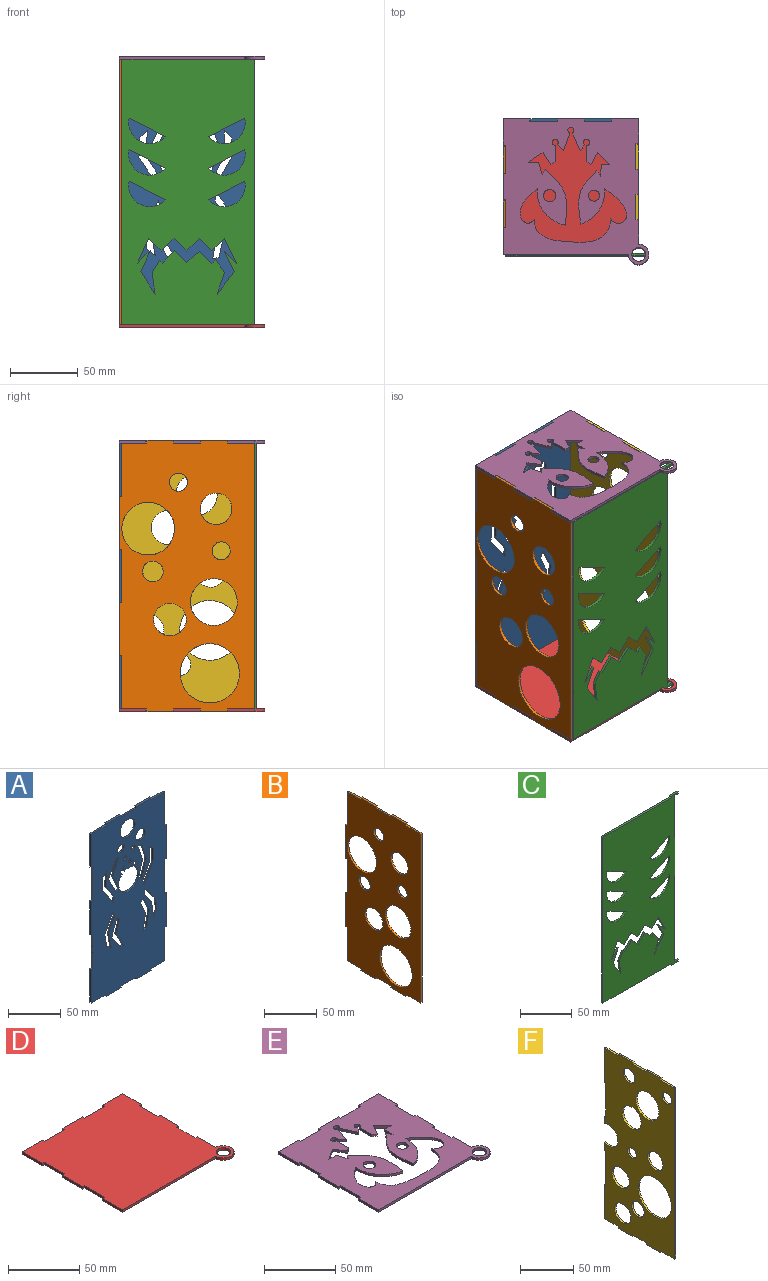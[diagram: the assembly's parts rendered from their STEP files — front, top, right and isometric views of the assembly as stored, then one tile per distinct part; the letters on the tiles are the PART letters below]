
ASSEMBLY  parts=6 mates=5
PART A: 102 faces, bbox 100x2x200 mm
  f0: plane 200x100mm, normal (0,-1,0), area 16666.3mm2, adj f2,f3,f4,f5,f6,f7,f8,f9
  f1: plane 200x100mm, normal (0,1,0), area 16666.3mm2, adj f2,f3,f4,f5,f6,f7,f8,f9
  f2: plane 39.2x2mm, normal (-1,0,0), area 78.4mm2, adj f0,f1,f33,f35
  f3: plane 39.2x2mm, normal (-1,0,0), area 78.4mm2, adj f0,f1,f16,f32
  f4: plane 39.6x2mm, normal (1,0,0), area 79.2mm2, adj f0,f1,f25,f28
  f5: plane 39.6x2mm, normal (1,0,0), area 79.2mm2, adj f0,f1,f26,f30
  f6: plane 17.8x2mm, normal (0,0,-1), area 35.6mm2, adj f0,f1,f15,f31
  f7: plane 39.2x2mm, normal (-1,0,0), area 78.4mm2, adj f0,f1,f24,f36
  f8: plane 20.4x2mm, normal (0,0,1), area 40.8mm2, adj f0,f1,f20,f23
  f9: plane 20.4x2mm, normal (0,0,1), area 40.8mm2, adj f0,f1,f18,f22
  f10: plane 20.4x2mm, normal (0,0,-1), area 40.8mm2, adj f0,f1,f12,f17
  f11: plane 20.4x2mm, normal (0,0,-1), area 40.8mm2, adj f0,f1,f14,f15
  f12: plane 2x2mm, normal (1,0,0), area 4mm2, adj f0,f1,f10,f13
  f13: plane 19.6x2mm, normal (0,0,-1), area 39.2mm2, adj f0,f1,f12,f14
  f14: plane 2x2mm, normal (-1,0,0), area 4mm2, adj f0,f1,f11,f13
  f15: plane 2x2mm, normal (1,0,0), area 4mm2, adj f0,f1,f6,f11
  f16: plane 19.8x2mm, normal (0,0,-1), area 39.6mm2, adj f0,f1,f3,f17
  f17: plane 2x2mm, normal (-1,0,0), area 4mm2, adj f0,f1,f10,f16
  f18: plane 2x2mm, normal (-1,0,0), area 4mm2, adj f0,f1,f9,f19
  f19: plane 19.6x2mm, normal (0,0,1), area 39.2mm2, adj f0,f1,f18,f20
  f20: plane 2x2mm, normal (1,0,0), area 4mm2, adj f0,f1,f8,f19
  f21: plane 17.8x2mm, normal (0,0,1), area 35.6mm2, adj f0,f1,f22,f29
  f22: plane 2x2mm, normal (1,0,0), area 4mm2, adj f0,f1,f9,f21
  f23: plane 2x2mm, normal (-1,0,0), area 4mm2, adj f0,f1,f8,f24
  f24: plane 19.8x2mm, normal (0,0,1), area 39.6mm2, adj f0,f1,f7,f23
  f25: plane 2x2mm, normal (0,0,-1), area 4mm2, adj f0,f1,f4,f27
  f26: plane 2x2mm, normal (0,0,1), area 4mm2, adj f0,f1,f5,f27
  f27: plane 38.8x2mm, normal (1,0,0), area 77.6mm2, adj f0,f1,f25,f26
  f28: plane 2x2mm, normal (0,0,1), area 4mm2, adj f0,f1,f4,f29
  f29: plane 39x2mm, normal (1,0,0), area 78mm2, adj f0,f1,f21,f28
  f30: plane 2x2mm, normal (0,0,-1), area 4mm2, adj f0,f1,f5,f31
  f31: plane 39x2mm, normal (1,0,0), area 78mm2, adj f0,f1,f6,f30
  f32: plane 2x2mm, normal (0,0,1), area 4mm2, adj f0,f1,f3,f34
  f33: plane 2x2mm, normal (0,0,-1), area 4mm2, adj f0,f1,f2,f34
  f34: plane 39.2x2mm, normal (-1,0,0), area 78.4mm2, adj f0,f1,f32,f33
  f35: plane 2x2mm, normal (0,0,1), area 4mm2, adj f0,f1,f2,f37
  f36: plane 2x2mm, normal (0,0,-1), area 4mm2, adj f0,f1,f7,f37
  f37: plane 39.2x2mm, normal (-1,0,0), area 78.4mm2, adj f0,f1,f35,f36
  f38: plane 4.08x3.06mm, normal (-0.8,0,0.6), area 10.2mm2, adj f0,f1,f39,f47
  f39: cylinder r=13.45mm len=26.89mm, axis (0,1,0), area 129.9mm2, adj f0,f1,f38,f40
  f40: plane 4.08x2.66mm, normal (0.84,0,0.55), area 9.7mm2, adj f0,f1,f39,f41
  f41: plane 6.45x5.23mm, normal (0.63,0,-0.78), area 16.6mm2, adj f0,f1,f40,f42
  f42: plane 5.68x2.93mm, normal (-0.89,0,0.46), area 12.8mm2, adj f0,f1,f41,f43
  f43: plane 2.68x2mm, normal (-0.46,0,-0.89), area 6mm2, adj f0,f1,f42,f44
  f44: cylinder r=13.45mm len=10.78mm, axis (0,1,0), area 22.2mm2, adj f0,f1,f43,f45
  f45: plane 2.61x2mm, normal (0.46,0,-0.89), area 5.9mm2, adj f0,f1,f44,f46
  f46: plane 5.68x2.98mm, normal (0.89,0,0.46), area 12.8mm2, adj f0,f1,f45,f47
  f47: plane 6.98x5.23mm, normal (-0.6,0,-0.8), area 17.4mm2, adj f0,f1,f38,f46
  f48: cylinder r=2.47mm len=4.94mm, axis (0,1,0), area 31.1mm2, adj f0,f1
  f49: cylinder r=2.82mm len=5.64mm, axis (0,1,0), area 35.4mm2, adj f0,f1
  f50: cylinder r=4.52mm len=9.03mm, axis (0,1,0), area 56.8mm2, adj f0,f1
  f51: cylinder r=10.15mm len=20.29mm, axis (0,1,0), area 127.5mm2, adj f0,f1
  f52: cylinder r=1.85mm len=3.69mm, axis (0,1,0), area 23.2mm2, adj f0,f1
  f53: cylinder r=6.54mm len=13.08mm, axis (0,1,0), area 82.2mm2, adj f0,f1
  f54: cylinder r=21.63mm len=3.26mm, axis (0,1,0), area 9mm2, adj f0,f1,f55,f59
  f55: plane 20.47x10.75mm, normal (0.89,0,0.46), area 46.2mm2, adj f0,f1,f54,f56
  f56: plane 18.83x9.64mm, normal (0.89,0,-0.46), area 42.3mm2, adj f0,f1,f55,f57
  f57: plane 4.3x2mm, normal (0.15,0,-0.99), area 8.7mm2, adj f0,f1,f56,f58
  f58: plane 18.83x8.03mm, normal (-0.92,0,0.39), area 40.9mm2, adj f0,f1,f57,f59
  f59: plane 18.05x8.1mm, normal (-0.91,0,-0.41), area 39.6mm2, adj f0,f1,f54,f58
  f60: cylinder r=21.63mm len=3.98mm, axis (0,1,0), area 11.3mm2, adj f0,f1,f61,f65
  f61: plane 18.05x5.28mm, normal (0.96,0,-0.28), area 37.6mm2, adj f0,f1,f60,f62
  f62: plane 18.83x6.04mm, normal (0.95,0,0.31), area 39.5mm2, adj f0,f1,f61,f63
  f63: plane 4.89x2mm, normal (-0.13,0,-0.99), area 9.9mm2, adj f0,f1,f62,f64
  f64: plane 18.83x6.47mm, normal (-0.95,0,-0.32), area 39.8mm2, adj f0,f1,f63,f65
  f65: plane 21.36x6.62mm, normal (-0.96,0,0.3), area 44.7mm2, adj f0,f1,f60,f64
  f66: plane 18.12x8.28mm, normal (-0.91,0,-0.42), area 39.8mm2, adj f0,f1,f67,f71
  f67: plane 19.5x4mm, normal (-0.98,0,0.2), area 39.8mm2, adj f0,f1,f66,f68
  f68: plane 4.77x2mm, normal (-0.26,0,0.97), area 9.9mm2, adj f0,f1,f67,f69
  f69: plane 19.45x3.58mm, normal (0.98,0,-0.18), area 39.5mm2, adj f0,f1,f68,f70
  f70: plane 14.53x6.36mm, normal (0.92,0,0.4), area 31.7mm2, adj f0,f1,f69,f71
  f71: cylinder r=21.63mm len=4.92mm, axis (0,1,0), area 11.9mm2, adj f0,f1,f66,f70
  f72: plane 19.04x14.27mm, normal (-0.8,0,-0.6), area 47.6mm2, adj f0,f1,f73,f77
  f73: plane 14.25x2mm, normal (-0.99,0,-0.13), area 28.7mm2, adj f0,f1,f72,f74
  f74: plane 5.85x4.73mm, normal (-0.78,0,0.63), area 15.1mm2, adj f0,f1,f73,f75
  f75: plane 18.75x2.42mm, normal (0.99,0,0.13), area 37.8mm2, adj f0,f1,f74,f76
  f76: plane 14.05x9.72mm, normal (0.82,0,0.57), area 34.2mm2, adj f0,f1,f75,f77
  f77: cylinder r=21.63mm len=6.34mm, axis (0,1,0), area 12.8mm2, adj f0,f1,f72,f76
  f78: cylinder r=21.63mm len=5.19mm, axis (0,1,0), area 11.2mm2, adj f0,f1,f79,f83
  f79: plane 16.73x8.65mm, normal (0.89,0,-0.46), area 37.7mm2, adj f0,f1,f78,f80
  f80: plane 18.91x2mm, normal (1,0,0), area 37.8mm2, adj f0,f1,f79,f81
  f81: plane 5.44x5.2mm, normal (-0.69,0,-0.72), area 15.1mm2, adj f0,f1,f80,f82
  f82: plane 14.37x2mm, normal (-1,0,0), area 28.7mm2, adj f0,f1,f81,f83
  f83: plane 21.27x12.03mm, normal (-0.87,0,0.49), area 48.9mm2, adj f0,f1,f78,f82
  f84: plane 14.38x2.62mm, normal (0.98,0,0.18), area 29.2mm2, adj f0,f1,f85,f89
  f85: plane 21.56x11.05mm, normal (0.89,0,-0.46), area 48.5mm2, adj f0,f1,f84,f86
  f86: cylinder r=21.63mm len=5.63mm, axis (0,1,0), area 12.2mm2, adj f0,f1,f85,f87
  f87: plane 16.15x8.13mm, normal (-0.89,0,0.45), area 36.2mm2, adj f0,f1,f86,f88
  f88: plane 18.63x3.4mm, normal (-0.98,0,-0.18), area 37.9mm2, adj f0,f1,f87,f89
  f89: plane 6.04x4.46mm, normal (0.59,0,0.8), area 15mm2, adj f0,f1,f84,f88
  f90: cylinder r=21.63mm len=5.19mm, axis (0,1,0), area 11.2mm2, adj f0,f1,f91,f95
  f91: plane 21.04x14.45mm, normal (0.82,0,0.57), area 51mm2, adj f0,f1,f90,f92
  f92: plane 14.6x2mm, normal (1,0,-0.05), area 29.2mm2, adj f0,f1,f91,f93
  f93: plane 5.42x5.2mm, normal (0.69,0,-0.72), area 15mm2, adj f0,f1,f92,f94
  f94: plane 18.91x2mm, normal (-1,0,0.05), area 37.9mm2, adj f0,f1,f93,f95
  f95: plane 16.73x11.31mm, normal (-0.83,0,-0.56), area 40.4mm2, adj f0,f1,f90,f94
  f96: plane 17.44x11.97mm, normal (0.82,0,0.57), area 42.3mm2, adj f0,f1,f97,f101
  f97: plane 19.14x7.1mm, normal (0.94,0,-0.35), area 40.8mm2, adj f0,f1,f96,f98
  f98: cylinder r=21.63mm len=3.67mm, axis (0,1,0), area 9.6mm2, adj f0,f1,f97,f99
  f99: plane 15.95x4.82mm, normal (-0.96,0,0.29), area 33.3mm2, adj f0,f1,f98,f100
  f100: plane 17.65x10.38mm, normal (-0.86,0,-0.51), area 40.9mm2, adj f0,f1,f99,f101
  f101: plane 4.35x2mm, normal (0.02,0,1), area 8.7mm2, adj f0,f1,f96,f100
PART B: 38 faces, bbox 2x100x200 mm
  f0: plane 39.6x2mm, normal (0,1,0), area 79.2mm2, adj f3,f4,f23,f29
  f1: plane 39.6x2mm, normal (0,1,0), area 79.2mm2, adj f3,f4,f25,f26
  f2: plane 17.8x2mm, normal (0,0,-1), area 35.6mm2, adj f3,f4,f13,f28
  f3: plane 200x100mm, normal (1,0,0), area 14548.8mm2, adj f0,f1,f2,f5,f6,f7,f8,f9
  f4: plane 200x100mm, normal (-1,0,0), area 14548.8mm2, adj f0,f1,f2,f5,f6,f7,f8,f9
  f5: plane 20.4x2mm, normal (0,0,1), area 40.8mm2, adj f3,f4,f18,f21
  f6: plane 20.4x2mm, normal (0,0,1), area 40.8mm2, adj f3,f4,f16,f20
  f7: plane 196x2mm, normal (0,-1,0), area 392mm2, adj f3,f4,f14,f22
  f8: plane 20.4x2mm, normal (0,0,-1), area 40.8mm2, adj f3,f4,f10,f15
  f9: plane 20.4x2mm, normal (0,0,-1), area 40.8mm2, adj f3,f4,f12,f13
  f10: plane 2x2mm, normal (0,1,0), area 4mm2, adj f3,f4,f8,f11
  f11: plane 19.6x2mm, normal (0,0,-1), area 39.2mm2, adj f3,f4,f10,f12
  f12: plane 2x2mm, normal (0,-1,0), area 4mm2, adj f3,f4,f9,f11
  f13: plane 2x2mm, normal (0,1,0), area 4mm2, adj f2,f3,f4,f9
  f14: plane 19.8x2mm, normal (0,0,-1), area 39.6mm2, adj f3,f4,f7,f15
  f15: plane 2x2mm, normal (0,-1,0), area 4mm2, adj f3,f4,f8,f14
  f16: plane 2x2mm, normal (0,-1,0), area 4mm2, adj f3,f4,f6,f17
  f17: plane 19.6x2mm, normal (0,0,1), area 39.2mm2, adj f3,f4,f16,f18
  f18: plane 2x2mm, normal (0,1,0), area 4mm2, adj f3,f4,f5,f17
  f19: plane 17.8x2mm, normal (0,0,1), area 35.6mm2, adj f3,f4,f20,f27
  f20: plane 2x2mm, normal (0,1,0), area 4mm2, adj f3,f4,f6,f19
  f21: plane 2x2mm, normal (0,-1,0), area 4mm2, adj f3,f4,f5,f22
  f22: plane 19.8x2mm, normal (0,0,1), area 39.6mm2, adj f3,f4,f7,f21
  f23: plane 2x2mm, normal (0,0,1), area 4mm2, adj f0,f3,f4,f24
  f24: plane 38.8x2mm, normal (0,1,0), area 77.6mm2, adj f3,f4,f23,f25
  f25: plane 2x2mm, normal (0,0,-1), area 4mm2, adj f1,f3,f4,f24
  f26: plane 2x2mm, normal (0,0,1), area 4mm2, adj f1,f3,f4,f27
  f27: plane 39x2mm, normal (0,1,0), area 78mm2, adj f3,f4,f19,f26
  f28: plane 39x2mm, normal (0,1,0), area 78mm2, adj f2,f3,f4,f29
  f29: plane 2x2mm, normal (0,0,-1), area 4mm2, adj f0,f3,f4,f28
  f30: cylinder r=11.7mm len=23.4mm, axis (-1,0,0), area 147mm2, adj f3,f4
  f31: cylinder r=7.63mm len=15.27mm, axis (-1,0,0), area 95.9mm2, adj f3,f4
  f32: cylinder r=17.3mm len=34.6mm, axis (-1,0,0), area 217.4mm2, adj f3,f4
  f33: cylinder r=21.87mm len=43.75mm, axis (-1,0,0), area 274.9mm2, adj f3,f4
  f34: cylinder r=19.45mm len=38.89mm, axis (-1,0,0), area 244.4mm2, adj f3,f4
  f35: cylinder r=6.71mm len=13.42mm, axis (-1,0,0), area 84.3mm2, adj f3,f4
  f36: cylinder r=6.6mm len=13.2mm, axis (-1,0,0), area 82.9mm2, adj f3,f4
  f37: cylinder r=12.07mm len=24.15mm, axis (-1,0,0), area 151.7mm2, adj f3,f4
PART C: 50 faces, bbox 103x2x200 mm
  f0: cylinder r=15.53mm len=27.04mm, axis (0,1,0), area 81.3mm2, adj f47,f48,f49
  f1: cylinder r=15.53mm len=27.04mm, axis (0,1,0), area 81.3mm2, adj f40,f48,f49
  f2: plane 16.09x5.46mm, normal (0.95,0,-0.32), area 34mm2, adj f3,f41,f48,f49
  f3: plane 9.4x6.49mm, normal (0.82,0,0.57), area 22.8mm2, adj f2,f4,f48,f49
  f4: plane 2.84x2.79mm, normal (-0.7,0,0.71), area 8mm2, adj f3,f5,f48,f49
  f5: plane 9.17x9.02mm, normal (0.71,0,0.7), area 25.7mm2, adj f4,f6,f48,f49
  f6: plane 9.45x8.73mm, normal (-0.68,0,0.73), area 25.7mm2, adj f5,f7,f48,f49
  f7: plane 8.97x8.82mm, normal (0.71,0,0.7), area 25.2mm2, adj f6,f8,f48,f49
  f8: plane 9.27x9.11mm, normal (-0.7,0,0.71), area 26mm2, adj f7,f9,f48,f49
  f9: plane 2.07x2.04mm, normal (0.71,0,0.7), area 5.8mm2, adj f8,f10,f48,f49
  f10: plane 8.98x5.53mm, normal (-0.85,0,0.52), area 21.1mm2, adj f9,f11,f48,f49
  f11: plane 16.09x2.22mm, normal (-0.99,0,-0.14), area 32.5mm2, adj f10,f12,f48,f49
  f12: plane 16.71x10.37mm, normal (0.85,0,0.53), area 39.3mm2, adj f11,f13,f48,f49
  f13: plane 15.41x6.75mm, normal (0.92,0,-0.4), area 33.6mm2, adj f12,f14,f48,f49
  f14: plane 9.27x9.11mm, normal (-0.7,0,0.71), area 26mm2, adj f13,f15,f48,f49
  f15: plane 18.28x8.1mm, normal (0.91,0,-0.41), area 40mm2, adj f14,f16,f48,f49
  f16: plane 9.42x9.26mm, normal (-0.71,0,-0.7), area 26.4mm2, adj f15,f17,f48,f49
  f17: plane 9.58x9.42mm, normal (0.7,0,-0.71), area 26.9mm2, adj f16,f18,f48,f49
  f18: plane 9.42x9.26mm, normal (-0.71,0,-0.7), area 26.4mm2, adj f17,f19,f48,f49
  f19: plane 9.58x9.42mm, normal (0.7,0,-0.71), area 26.9mm2, adj f18,f20,f48,f49
  f20: plane 9.17x9.02mm, normal (-0.71,0,-0.7), area 25.7mm2, adj f19,f21,f48,f49
  f21: plane 9.33x9.17mm, normal (0.7,0,-0.71), area 26.2mm2, adj f20,f22,f48,f49
  f22: plane 18.59x9.02mm, normal (-0.9,0,-0.44), area 41.3mm2, adj f21,f23,f48,f49
  f23: plane 9.17x9.02mm, normal (0.71,0,0.7), area 25.7mm2, adj f22,f24,f48,f49
  f24: plane 15.16x7.35mm, normal (-0.9,0,-0.44), area 33.7mm2, adj f23,f41,f48,f49
  f25: cylinder r=15.53mm len=27.04mm, axis (0,1,0), area 81.3mm2, adj f42,f48,f49
  f26: cylinder r=15.53mm len=27.04mm, axis (0,1,0), area 81.3mm2, adj f43,f48,f49
  f27: cylinder r=15.53mm len=27.04mm, axis (0,1,0), area 81.3mm2, adj f44,f48,f49
  f28: cylinder r=15.53mm len=27.04mm, axis (0,1,0), area 81.3mm2, adj f45,f48,f49
  f29: plane 2x1.99mm, normal (-1,0,0), area 4mm2, adj f30,f46,f48,f49
  f30: plane 92.95x2mm, normal (0,0,1), area 185.9mm2, adj f29,f31,f48,f49
  f31: plane 196x2mm, normal (-1,0,0), area 392mm2, adj f30,f32,f48,f49
  f32: plane 93x2mm, normal (0,0,-1), area 186mm2, adj f31,f33,f48,f49
  f33: plane 2x2mm, normal (-1,0,0), area 4mm2, adj f32,f34,f48,f49
  f34: plane 10x2mm, normal (0,0,-1), area 20mm2, adj f33,f35,f48,f49
  f35: plane 2x2mm, normal (1,0,0), area 4mm2, adj f34,f36,f48,f49
  f36: plane 4.86x2mm, normal (0,0,1), area 9.7mm2, adj f35,f37,f48,f49
  f37: plane 196x2mm, normal (1,0,0), area 392mm2, adj f36,f38,f48,f49
  f38: plane 4.81x2mm, normal (0,0,-1), area 9.6mm2, adj f37,f39,f48,f49
  f39: plane 2x1.99mm, normal (1,0,0), area 4mm2, adj f38,f46,f48,f49
  f40: plane 26.69x13.7mm, normal (-0.46,0,-0.89), area 60mm2, adj f1,f48,f49
  f41: plane 16.71x12.81mm, normal (-0.79,0,0.61), area 42.1mm2, adj f2,f24,f48,f49
  f42: plane 26.69x13.7mm, normal (0.46,0,-0.89), area 60mm2, adj f25,f48,f49
  f43: plane 26.69x13.7mm, normal (0.46,0,-0.89), area 60mm2, adj f26,f48,f49
  f44: plane 26.69x13.7mm, normal (0.46,0,-0.89), area 60mm2, adj f27,f48,f49
  f45: plane 26.69x13.7mm, normal (-0.46,0,-0.89), area 60mm2, adj f28,f48,f49
  f46: plane 10x2mm, normal (0,0,1), area 20mm2, adj f29,f39,f48,f49
  f47: plane 26.69x13.7mm, normal (-0.46,0,-0.89), area 60mm2, adj f0,f48,f49
  f48: plane 199.99x103mm, normal (0,-1,0), area 16804.6mm2, adj f0,f1,f2,f3,f4,f5,f6,f7
  f49: plane 199.99x103mm, normal (0,1,0), area 16804.6mm2, adj f0,f1,f2,f3,f4,f5,f6,f7
PART D: 32 faces, bbox 107.5x107.5x2 mm
  f0: plane 20x2mm, normal (-1,0,0), area 40mm2, adj f12,f13,f27,f29
  f1: plane 20x2mm, normal (-1,0,0), area 40mm2, adj f9,f12,f13,f26
  f2: plane 20x2mm, normal (0,1,0), area 40mm2, adj f12,f13,f21,f23
  f3: plane 20x2mm, normal (0,1,0), area 40mm2, adj f8,f12,f13,f20
  f4: plane 18.55x2mm, normal (1,0,0), area 37.1mm2, adj f12,f13,f16,f17
  f5: plane 18.28x2mm, normal (1,0,0), area 36.6mm2, adj f10,f12,f13,f14
  f6: plane 18.55x2mm, normal (1,0,0), area 37.1mm2, adj f7,f12,f13,f19
  f7: plane 20x2mm, normal (0,1,0), area 40mm2, adj f6,f12,f13,f24
  f8: plane 20x2mm, normal (-1,0,0), area 40mm2, adj f3,f12,f13,f30
  f9: plane 92.5x2mm, normal (0,-1,0), area 185mm2, adj f1,f10,f12,f13
  f10: cylinder r=7.5mm len=15mm, axis (0,0,-1), area 70.7mm2, adj f5,f9,f12,f13
  f11: cylinder r=5mm len=10mm, axis (0,0,-1), area 62.8mm2, adj f12,f13
  f12: plane 107.5x107.5mm, normal (0,0,1), area 9819.8mm2, adj f0,f1,f2,f3,f4,f5,f6,f7
  f13: plane 107.5x107.5mm, normal (0,0,-1), area 9819.8mm2, adj f0,f1,f2,f3,f4,f5,f6,f7
  f14: plane 2x2mm, normal (0,1,0), area 4mm2, adj f5,f12,f13,f15
  f15: plane 18.55x2mm, normal (1,0,0), area 37.1mm2, adj f12,f13,f14,f16
  f16: plane 2x2mm, normal (0,-1,0), area 4mm2, adj f4,f12,f13,f15
  f17: plane 2x2mm, normal (0,1,0), area 4mm2, adj f4,f12,f13,f18
  f18: plane 18.55x2mm, normal (1,0,0), area 37.1mm2, adj f12,f13,f17,f19
  f19: plane 2x2mm, normal (0,-1,0), area 4mm2, adj f6,f12,f13,f18
  f20: plane 2x2mm, normal (1,0,0), area 4mm2, adj f3,f12,f13,f22
  f21: plane 2x2mm, normal (-1,0,0), area 4mm2, adj f2,f12,f13,f22
  f22: plane 20x2mm, normal (0,1,0), area 40mm2, adj f12,f13,f20,f21
  f23: plane 2x2mm, normal (1,0,0), area 4mm2, adj f2,f12,f13,f25
  f24: plane 2x2mm, normal (-1,0,0), area 4mm2, adj f7,f12,f13,f25
  f25: plane 20x2mm, normal (0,1,0), area 40mm2, adj f12,f13,f23,f24
  f26: plane 2x2mm, normal (0,1,0), area 4mm2, adj f1,f12,f13,f28
  f27: plane 2x2mm, normal (0,-1,0), area 4mm2, adj f0,f12,f13,f28
  f28: plane 20x2mm, normal (-1,0,0), area 40mm2, adj f12,f13,f26,f27
  f29: plane 2x2mm, normal (0,1,0), area 4mm2, adj f0,f12,f13,f31
  f30: plane 2x2mm, normal (0,-1,0), area 4mm2, adj f8,f12,f13,f31
  f31: plane 20x2mm, normal (-1,0,0), area 40mm2, adj f12,f13,f29,f30
PART E: 62 faces, bbox 107.5x107.5x2 mm
  f0: plane 20x2mm, normal (-1,0,0), area 40mm2, adj f2,f3,f9,f30
  f1: plane 20x2mm, normal (-1,0,0), area 40mm2, adj f2,f3,f27,f29
  f2: plane 107.52x107.52mm, normal (0,0,-1), area 7012.3mm2, adj f0,f1,f4,f5,f6,f7,f8,f9
  f3: plane 107.52x107.52mm, normal (0,0,1), area 7012.3mm2, adj f0,f1,f4,f5,f6,f7,f8,f9
  f4: plane 20x2mm, normal (0,1,0), area 40mm2, adj f2,f3,f8,f24
  f5: plane 20x2mm, normal (0,1,0), area 40mm2, adj f2,f3,f21,f23
  f6: plane 18.26x2mm, normal (1,0,0), area 36.5mm2, adj f2,f3,f10,f19
  f7: plane 18.55x2mm, normal (1,0,0), area 37.1mm2, adj f2,f3,f16,f17
  f8: plane 20x2mm, normal (-1,0,0), area 40mm2, adj f2,f3,f4,f26
  f9: plane 92.48x2mm, normal (0,-1,0), area 185mm2, adj f0,f2,f3,f10
  f10: cylinder r=7.52mm len=15.04mm, axis (0,0,1), area 70.9mm2, adj f2,f3,f6,f9
  f11: plane 18.55x2mm, normal (1,0,0), area 37.1mm2, adj f2,f3,f12,f14
  f12: plane 20x2mm, normal (0,1,0), area 40mm2, adj f2,f3,f11,f20
  f13: cylinder r=5.01mm len=10.03mm, axis (0,0,1), area 63mm2, adj f2,f3
  f14: plane 2x2mm, normal (0,-1,0), area 4mm2, adj f2,f3,f11,f15
  f15: plane 18.55x2mm, normal (1,0,0), area 37.1mm2, adj f2,f3,f14,f16
  f16: plane 2x2mm, normal (0,1,0), area 4mm2, adj f2,f3,f7,f15
  f17: plane 2x2mm, normal (0,-1,0), area 4mm2, adj f2,f3,f7,f18
  f18: plane 18.55x2mm, normal (1,0,0), area 37.1mm2, adj f2,f3,f17,f19
  f19: plane 2x2mm, normal (0,1,0), area 4mm2, adj f2,f3,f6,f18
  f20: plane 2x2mm, normal (-1,0,0), area 4mm2, adj f2,f3,f12,f22
  f21: plane 2x2mm, normal (1,0,0), area 4mm2, adj f2,f3,f5,f22
  f22: plane 20x2mm, normal (0,1,0), area 40mm2, adj f2,f3,f20,f21
  f23: plane 2x2mm, normal (-1,0,0), area 4mm2, adj f2,f3,f5,f25
  f24: plane 2x2mm, normal (1,0,0), area 4mm2, adj f2,f3,f4,f25
  f25: plane 20x2mm, normal (0,1,0), area 40mm2, adj f2,f3,f23,f24
  f26: plane 2x2mm, normal (0,-1,0), area 4mm2, adj f2,f3,f8,f28
  f27: plane 2x2mm, normal (0,1,0), area 4mm2, adj f1,f2,f3,f28
  f28: plane 20x2mm, normal (-1,0,0), area 40mm2, adj f2,f3,f26,f27
  f29: plane 2x2mm, normal (0,-1,0), area 4mm2, adj f1,f2,f3,f31
  f30: plane 2x2mm, normal (0,1,0), area 4mm2, adj f0,f2,f3,f31
  f31: plane 20x2mm, normal (-1,0,0), area 40mm2, adj f2,f3,f29,f30
  f32: cylinder r=2.27mm len=4.54mm, axis (0,0,1), area 25.6mm2, adj f2,f3,f33,f59
  f33: plane 4.34x3.25mm, normal (0.8,-0.6,0), area 10.8mm2, adj f2,f3,f32,f34
  f34: plane 13.05x6.01mm, normal (-0.91,-0.42,0), area 28.7mm2, adj f2,f3,f33,f35
  f35: cylinder r=2.26mm len=4.53mm, axis (0,0,1), area 24.9mm2, adj f2,f3,f34,f36
  f36: plane 12.98x4.79mm, normal (0.94,-0.35,0), area 27.7mm2, adj f2,f3,f35,f37
  f37: plane 4.55x4.43mm, normal (-0.72,-0.7,0), area 12.7mm2, adj f2,f3,f36,f38
  f38: cylinder r=2.24mm len=4.49mm, axis (0,0,1), area 24.7mm2, adj f2,f3,f37,f39
  f39: plane 12.27x2mm, normal (1,0,0), area 24.5mm2, adj f2,f3,f38,f40
  f40: cylinder r=24.87mm len=3.19mm, axis (0,0,1), area 7.5mm2, adj f2,f3,f39,f41
  f41: plane 9x5.82mm, normal (-0.84,-0.54,0), area 21.4mm2, adj f2,f3,f40,f42
  f42: plane 10.96x7.1mm, normal (0.54,-0.84,0), area 26.1mm2, adj f2,f3,f41,f43
  f43: plane 7.77x2mm, normal (0,1,0), area 15.5mm2, adj f2,f3,f42,f44
  f44: plane 9.11x2.47mm, normal (0.97,0.26,0), area 18.9mm2, adj f2,f3,f43,f45
  f45: cylinder r=24.87mm len=3.9mm, axis (0,0,1), area 9.7mm2, adj f2,f3,f44,f46
  f46: extruded ~41.22x15.21mm, area 92.7mm2, adj f2,f3,f45,f47
  f47: cylinder r=24.87mm len=26.67mm, axis (0,0,1), area 74mm2, adj f2,f3,f46,f48
  f48: extruded ~25.4x12.71mm, area 77.7mm2, adj f2,f3,f47,f49
  f49: extruded ~56.07x17.4mm, area 149.6mm2, adj f2,f3,f48,f50
  f50: extruded ~25.53x16.36mm, area 86.1mm2, adj f2,f3,f49,f51
  f51: cylinder r=24.87mm len=25.95mm, axis (0,0,1), area 67.8mm2, adj f2,f3,f50,f52
  f52: extruded ~39.57x13.48mm, area 88.1mm2, adj f2,f3,f51,f53
  f53: cylinder r=24.87mm len=4.24mm, axis (0,0,1), area 10.2mm2, adj f2,f3,f52,f54
  f54: plane 8.48x2mm, normal (-1,0.04,0), area 17mm2, adj f2,f3,f53,f55
  f55: plane 6.25x2mm, normal (0,1,0), area 12.5mm2, adj f2,f3,f54,f56
  f56: plane 9x8.91mm, normal (-0.71,-0.7,0), area 25.3mm2, adj f2,f3,f55,f57
  f57: plane 9x4.92mm, normal (0.88,-0.48,0), area 20.5mm2, adj f2,f3,f56,f58
  f58: cylinder r=24.87mm len=3.19mm, axis (0,0,1), area 7.5mm2, adj f2,f3,f57,f59
  f59: plane 12.25x2mm, normal (-1,0,0), area 24.5mm2, adj f2,f3,f32,f58
  f60: cylinder r=4.1mm len=8.2mm, axis (0,0,1), area 51.5mm2, adj f2,f3
  f61: cylinder r=4.48mm len=8.97mm, axis (0,0,1), area 56.4mm2, adj f2,f3
PART F: 42 faces, bbox 2x92.8x200 mm
  f0: plane 9.37x2mm, normal (0,1,0), area 18.7mm2, adj f3,f4,f28,f32
  f1: plane 8.69x2mm, normal (0,1,0), area 17.4mm2, adj f3,f4,f26,f32
  f2: plane 39.2x2mm, normal (0,1,0), area 78.4mm2, adj f3,f4,f23,f25
  f3: plane 200x92.5mm, normal (1,0,0), area 13264.8mm2, adj f0,f1,f2,f5,f6,f7,f8,f9
  f4: plane 200x92.77mm, normal (-1,0,0), area 13318mm2, adj f0,f1,f2,f5,f6,f7,f8,f9
  f5: cylinder r=7.5mm len=196mm, axis (0,0,-1), area 396.8mm2, adj f3,f4,f12,f19
  f6: plane 18.95x2mm, normal (0,0,1), area 37.9mm2, adj f3,f4,f18,f22
  f7: plane 18.95x2mm, normal (0,0,1), area 37.9mm2, adj f3,f4,f20,f24
  f8: plane 39.2x2mm, normal (0,1,0), area 78.4mm2, adj f3,f4,f17,f29
  f9: plane 18.95x2mm, normal (0,0,-1), area 37.9mm2, adj f3,f4,f11,f13
  f10: plane 18.95x2mm, normal (0,0,-1), area 37.9mm2, adj f3,f4,f15,f16
  f11: plane 2x2mm, normal (0,-1,0), area 4mm2, adj f3,f4,f9,f12
  f12: plane 18.35x2mm, normal (0,0,-1), area 36.3mm2, adj f3,f4,f5,f11
  f13: plane 2x2mm, normal (0,1,0), area 4mm2, adj f3,f4,f9,f14
  f14: plane 18.15x2mm, normal (0,0,-1), area 36.3mm2, adj f3,f4,f13,f15
  f15: plane 2x2mm, normal (0,-1,0), area 4mm2, adj f3,f4,f10,f14
  f16: plane 2x2mm, normal (0,1,0), area 4mm2, adj f3,f4,f10,f17
  f17: plane 18.35x2mm, normal (0,0,-1), area 36.7mm2, adj f3,f4,f8,f16
  f18: plane 2x2mm, normal (0,-1,0), area 4mm2, adj f3,f4,f6,f19
  f19: plane 18.35x2mm, normal (0,0,1), area 36.3mm2, adj f3,f4,f5,f18
  f20: plane 2x2mm, normal (0,-1,0), area 4mm2, adj f3,f4,f7,f21
  f21: plane 18.15x2mm, normal (0,0,1), area 36.3mm2, adj f3,f4,f20,f22
  f22: plane 2x2mm, normal (0,1,0), area 4mm2, adj f3,f4,f6,f21
  f23: plane 18.35x2mm, normal (0,0,1), area 36.7mm2, adj f2,f3,f4,f24
  f24: plane 2x2mm, normal (0,1,0), area 4mm2, adj f3,f4,f7,f23
  f25: plane 2x2mm, normal (0,0,-1), area 4mm2, adj f2,f3,f4,f27
  f26: plane 2x2mm, normal (0,0,1), area 4mm2, adj f1,f3,f4,f27
  f27: plane 39.2x2mm, normal (0,1,0), area 78.4mm2, adj f3,f4,f25,f26
  f28: plane 2x2mm, normal (0,0,-1), area 4mm2, adj f0,f3,f4,f30
  f29: plane 2x2mm, normal (0,0,1), area 4mm2, adj f3,f4,f8,f30
  f30: plane 39.2x2mm, normal (0,1,0), area 78.4mm2, adj f3,f4,f28,f29
  f31: cylinder r=6.28mm len=12.56mm, axis (1,0,0), area 78.9mm2, adj f3,f4
  f32: cylinder r=12.09mm len=24.18mm, axis (1,0,0), area 100.4mm2, adj f0,f1,f3,f4
  f33: cylinder r=10.87mm len=21.74mm, axis (1,0,0), area 136.6mm2, adj f3,f4
  f34: cylinder r=7.85mm len=15.7mm, axis (1,0,0), area 98.7mm2, adj f3,f4
  f35: cylinder r=12.51mm len=25.02mm, axis (1,0,0), area 157.2mm2, adj f3,f4
  f36: cylinder r=10.08mm len=20.17mm, axis (1,0,0), area 126.7mm2, adj f3,f4
  f37: cylinder r=15.34mm len=30.68mm, axis (1,0,0), area 192.8mm2, adj f3,f4
  f38: cylinder r=8.22mm len=16.44mm, axis (1,0,0), area 103.3mm2, adj f3,f4
  f39: cylinder r=11.42mm len=22.85mm, axis (1,0,0), area 143.6mm2, adj f3,f4
  f40: cylinder r=22.06mm len=44.12mm, axis (1,0,0), area 277.2mm2, adj f3,f4
  f41: cylinder r=5.76mm len=11.53mm, axis (1,0,0), area 72.4mm2, adj f3,f4
PLACE A t=(-24.34,-78.87,47.77)mm
PLACE B t=(-24.34,-78.87,47.77)mm
PLACE C t=(-24.29,-78.87,47.78)mm
PLACE D t=(-24.34,-78.87,47.77)mm
PLACE E t=(-24.34,-78.87,47.77)mm
PLACE F t=(-24.34,-78.87,47.77)mm
MATE revolute E.f10 <-> C.f46  axis (0,0,1) through (25.66,-128.87,247.77)mm
MATE fastened D.f12 <-> A.f13  axis (0,0,1) through (-24.34,-28.87,49.77)mm
MATE fastened A.f19 <-> E.f2  axis (0,0,1) through (-24.34,-28.87,245.77)mm
MATE fastened A.f0 <-> F.f30  axis (0,-1,0) through (25.66,-30.87,108.57)mm
MATE fastened B.f24 <-> A.f0  axis (0,1,0) through (-74.34,-30.87,147.77)mm
